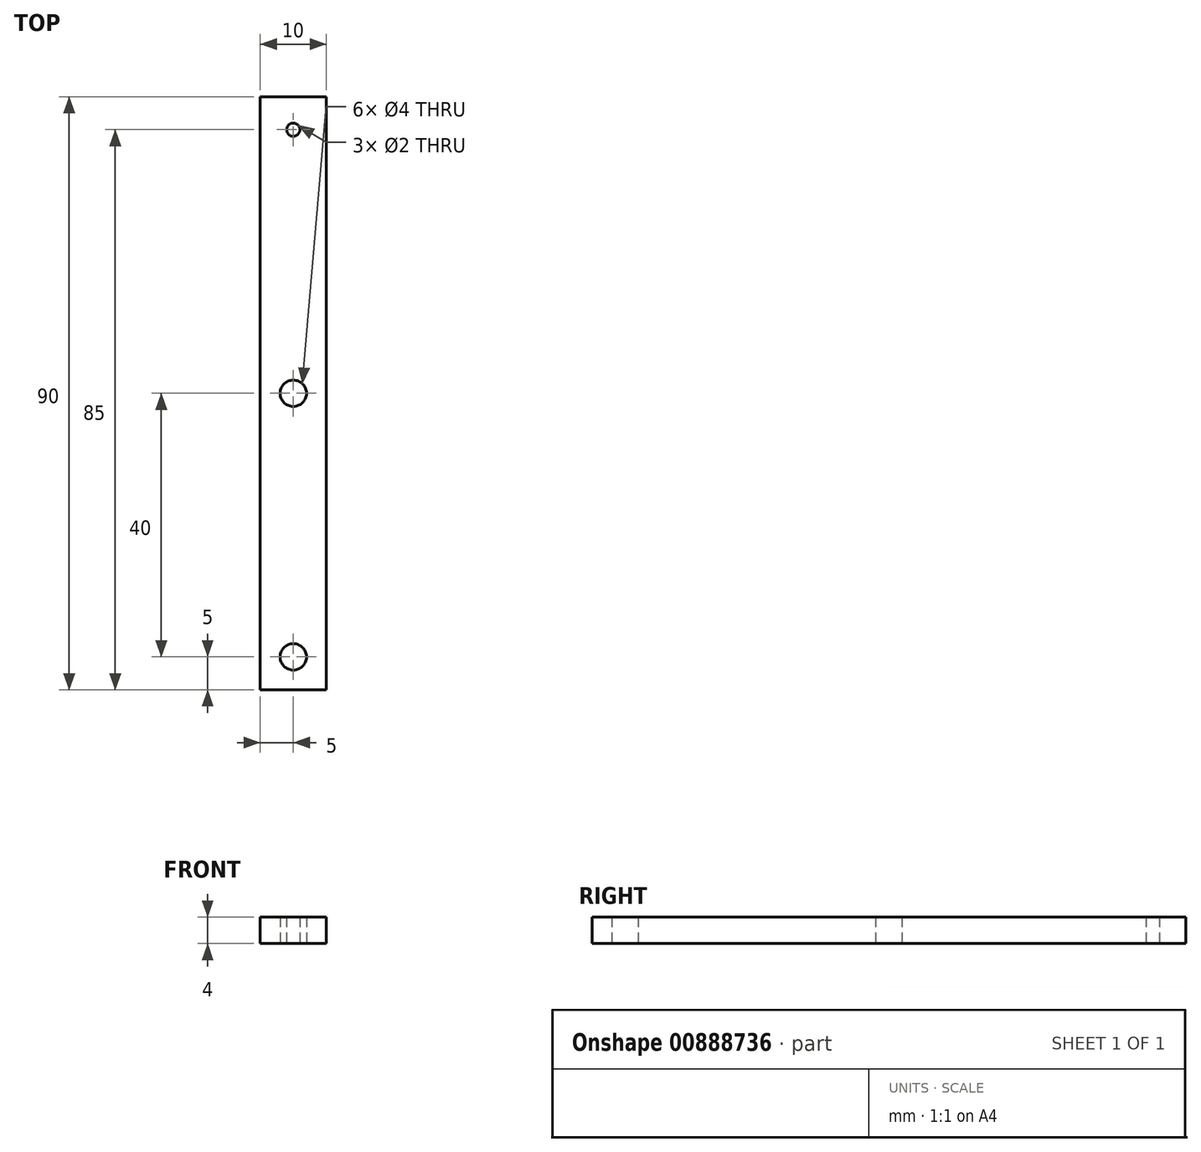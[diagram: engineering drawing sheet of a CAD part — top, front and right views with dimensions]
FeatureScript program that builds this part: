
annotation { "Feature Type Name" : "Feature", "Feature Type Description" : "" }
export const myFeature = defineFeature(function(context is Context, id is Id, definition is map)
    precondition{}
    {
        {
            var Q0;
            Q0=qCreatedBy(makeId("Top.planeOp"),FACE);
            var sketch = newSketch(context, id + "F0", { "sketchPlane" : qUnion([Q0])});
            skCircle(sketch, "E0", {"center": v(0, 0) * mm, "radius": 2 * mm});
            skCircle(sketch, "E1", {"center": v(0, 40) * mm, "radius": 2 * mm});
            skLineSegment(sketch, "E2.bottom", {"start": v(-5, 85) * mm, "end": v(5, 85) * mm});
            skLineSegment(sketch, "E2.top", {"start": v(-5, -5) * mm, "end": v(5, -5) * mm});
            skLineSegment(sketch, "E2.left", {"start": v(-5, 85) * mm, "end": v(-5, -5) * mm});
            skLineSegment(sketch, "E2.right", {"start": v(5, 85) * mm, "end": v(5, -5) * mm});
            skCircle(sketch, "E3", {"center": v(0, 80) * mm, "radius": 1 * mm});
            skPoint(sketch, "E4", {"position": v(0, -5) * mm});
            skPoint(sketch, "E5", {"position": v(-5, 40) * mm});
            skSolve(sketch);
        }
        {
            var Q0;
            Q0 = qSketchRegion(id + "F0", true);
            extrude(context, id + "F1", {"entities" : qUnion([Q0]), "endBound" : BoundingType.SYMMETRIC, "depth" : 4 * mm, "offsetDistance" : 25 * mm});
        }
    });
